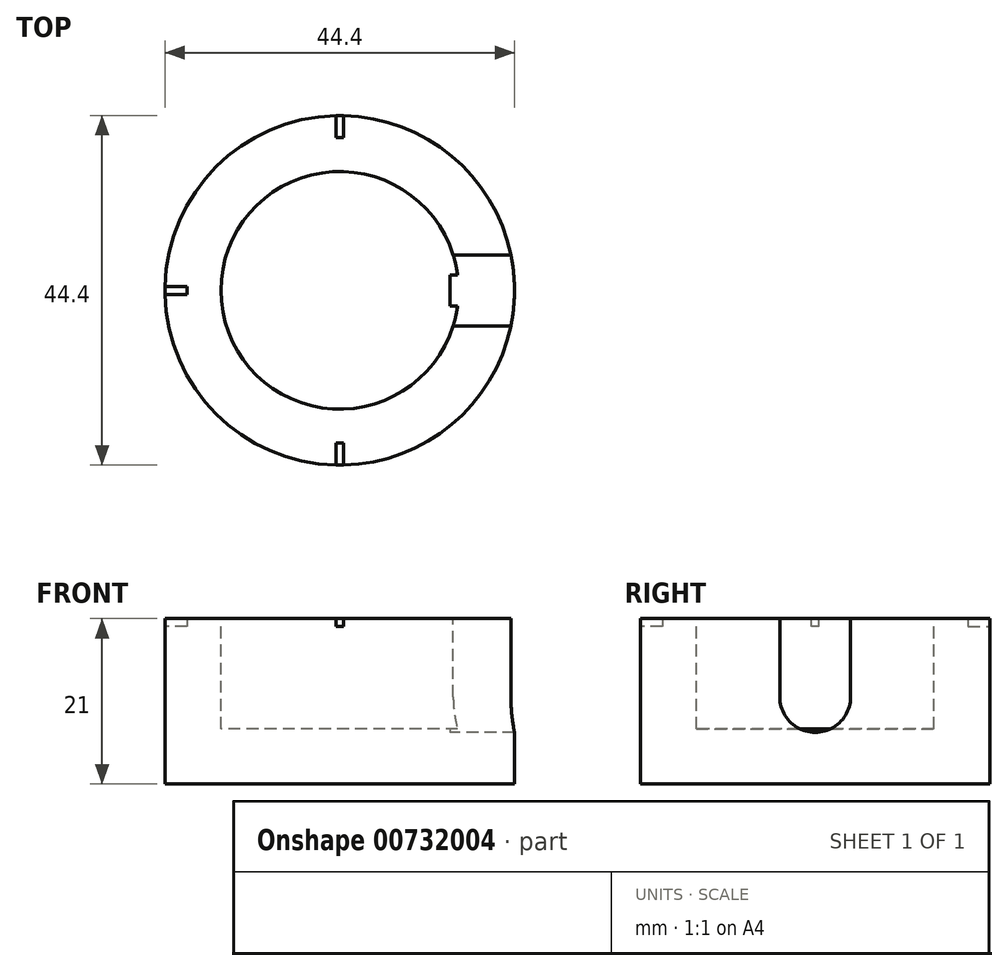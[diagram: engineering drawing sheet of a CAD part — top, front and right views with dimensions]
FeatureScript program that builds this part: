
annotation { "Feature Type Name" : "Feature", "Feature Type Description" : "" }
export const myFeature = defineFeature(function(context is Context, id is Id, definition is map)
    precondition{}
    {
        {
            var Q0;
            Q0=qCreatedBy(makeId("Front.planeOp"),FACE);
            var sketch = newSketch(context, id + "F0", { "sketchPlane" : qUnion([Q0])});
            skLineSegment(sketch, "E0", {"start": v(0, 0) * mm, "end": v(22.2, 0) * mm});
            skLineSegment(sketch, "E1", {"start": v(22.2, 0) * mm, "end": v(22.2, 21) * mm});
            skLineSegment(sketch, "E2", {"start": v(22.2, 21) * mm, "end": v(15.1, 21) * mm});
            skLineSegment(sketch, "E3", {"start": v(15.1, 21) * mm, "end": v(15.1, 7) * mm});
            skLineSegment(sketch, "E4", {"start": v(15.1, 7) * mm, "end": v(0, 7) * mm});
            skLineSegment(sketch, "E5", {"start": v(0, 7) * mm, "end": v(0, 0) * mm});
            skSolve(sketch);
        }
        {
            var Q0;
            Q0=qCreatedBy(makeId("Right.planeOp"),FACE);
            var sketch = newSketch(context, id + "F1", { "sketchPlane" : qUnion([Q0])});
            skLineSegment(sketch, "E6", {"start": v(0, 21.05) * mm, "end": v(-4.5, 21.05) * mm});
            skLineSegment(sketch, "E7", {"start": v(4.5, 21.05) * mm, "end": v(0, 21.05) * mm});
            skLineSegment(sketch, "E8", {"start": v(4.5, 21.05) * mm, "end": v(4.5, 11.05) * mm});
            skLineSegment(sketch, "E9", {"start": v(-4.5, 21.05) * mm, "end": v(-4.5, 11.05) * mm});
            skArc(sketch, "E10", {"start": v(4.5, 11.05) * mm, "mid": v(0, 6.55) * mm, "end": v(-4.5, 11.05) * mm});
            skSolve(sketch);
        }
        {
            var Q0;
            Q0=qCreatedBy(makeId("Top.planeOp"),FACE);
            var sketch = newSketch(context, id + "F2", { "sketchPlane" : qUnion([Q0])});
            skLineSegment(sketch, "E11", {"start": v(0, -19.4) * mm, "end": v(0.5, -19.4) * mm});
            skLineSegment(sketch, "E12", {"start": v(0.5, -19.4) * mm, "end": v(0.5, -22.4) * mm});
            skLineSegment(sketch, "E13", {"start": v(0.5, -22.4) * mm, "end": v(-0.5, -22.4) * mm});
            skLineSegment(sketch, "E14", {"start": v(-0.5, -22.4) * mm, "end": v(-0.5, -19.4) * mm});
            skLineSegment(sketch, "E15", {"start": v(-0.5, -19.4) * mm, "end": v(0, -19.4) * mm});
            skLineSegment(sketch, "E16", {"start": v(0, 22.42) * mm, "end": v(0.5, 22.42) * mm});
            skLineSegment(sketch, "E17", {"start": v(0.5, 22.42) * mm, "end": v(0.5, 19.42) * mm});
            skLineSegment(sketch, "E18", {"start": v(0.5, 19.42) * mm, "end": v(-0.5, 19.42) * mm});
            skLineSegment(sketch, "E19", {"start": v(-0.5, 19.42) * mm, "end": v(-0.5, 22.42) * mm});
            skLineSegment(sketch, "E20", {"start": v(-0.5, 22.42) * mm, "end": v(0, 22.42) * mm});
            skLineSegment(sketch, "E21", {"start": v(22.4, 0) * mm, "end": v(22.4, -0.5) * mm});
            skLineSegment(sketch, "E22", {"start": v(22.4, -0.5) * mm, "end": v(19.4, -0.5) * mm});
            skLineSegment(sketch, "E23", {"start": v(19.4, -0.5) * mm, "end": v(19.4, 0.5) * mm});
            skLineSegment(sketch, "E24", {"start": v(19.4, 0.5) * mm, "end": v(22.4, 0.5) * mm});
            skLineSegment(sketch, "E25", {"start": v(22.4, 0.5) * mm, "end": v(22.4, 0) * mm});
            skLineSegment(sketch, "E26", {"start": v(-19.4, 0) * mm, "end": v(-19.4, -0.5) * mm});
            skLineSegment(sketch, "E27", {"start": v(-19.4, -0.5) * mm, "end": v(-22.4, -0.5) * mm});
            skLineSegment(sketch, "E28", {"start": v(-22.4, -0.5) * mm, "end": v(-22.4, 0.5) * mm});
            skLineSegment(sketch, "E29", {"start": v(-22.4, 0.5) * mm, "end": v(-19.4, 0.5) * mm});
            skLineSegment(sketch, "E30", {"start": v(-19.4, 0.5) * mm, "end": v(-19.4, 0) * mm});
            skSolve(sketch);
        }
        {
            var Q0;
            Q0=makeQuery(id+"F0.imprint","IMPRINT",FACE,{"disambiguationData":[TD([[makeQuery(id+"F0.imprint","IMPRINT",EDGE,{"derivedFrom":sQuery(id+"F0.wireOp",EDGE,"E0")}),1.0]])]});
            var Q1;
            Q1=sQuery(id+"F0.wireOp",EDGE,"E5");
            revolve(context, id + "F3", {"surfaceOperationType" : NewSurfaceOperationType.NEW, "entities" : qUnion([Q0]), "axis" : qUnion([Q1]), "revolveType" : RevolveType.FULL});
        }
        {
            var Q0;
            Q0=makeQuery(id+"F1.imprint","IMPRINT",FACE,{"disambiguationData":[TD([[makeQuery(id+"F1.imprint","IMPRINT",EDGE,{"derivedFrom":sQuery(id+"F1.wireOp",EDGE,"E6")}),1.0]])]});
            extrude(context, id + "F4", {"entities" : qUnion([Q0]), "operationType" : NewBodyOperationType.REMOVE, "depth" : 30 * mm, "offsetDistance" : 25 * mm, "hasSecondDirection" : true, "secondDirectionOppositeDirection" : true, "secondDirectionDepth" : -14 * mm});
        }
        {
            var Q0;
            Q0 = qSketchRegion(id + "F2", true);
            var Q1;
            Q1=sQuery(id+"F2.wireOp",EDGE,"E13");
            var Q2;
            Q2=sQuery(id+"F2.wireOp",EDGE,"E17");
            var Q3;
            Q3=sQuery(id+"F2.wireOp",EDGE,"E18");
            var Q4;
            Q4=sQuery(id+"F2.wireOp",EDGE,"E12");
            var Q5;
            Q5=sQuery(id+"F2.wireOp",EDGE,"E14");
            var Q6;
            Q6=sQuery(id+"F2.wireOp",EDGE,"E19");
            var Q7;
            Q7=sQuery(id+"F2.wireOp",EDGE,"E27");
            var Q8;
            Q8=sQuery(id+"F2.wireOp",EDGE,"E29");
            var Q9;
            Q9=sQuery(id+"F2.wireOp",EDGE,"E24");
            var Q10;
            Q10=sQuery(id+"F2.wireOp",EDGE,"E22");
            var Q11;
            Q11=sQuery(id+"F2.wireOp",EDGE,"E28");
            var Q12;
            Q12=sQuery(id+"F2.wireOp",EDGE,"E23");
            var Q13;
            Q13=sQuery(id+"F2.wireOp",EDGE,"E25");
            var Q14;
            Q14=sQuery(id+"F2.wireOp",EDGE,"E16");
            var Q15;
            Q15=sQuery(id+"F2.wireOp",EDGE,"E15");
            var Q16;
            Q16=sQuery(id+"F2.wireOp",EDGE,"E11");
            var Q17;
            Q17=sQuery(id+"F2.wireOp",EDGE,"E20");
            var Q18;
            Q18=sQuery(id+"F2.wireOp",EDGE,"E30");
            var Q19;
            Q19=sQuery(id+"F2.wireOp",EDGE,"E21");
            var Q20;
            Q20=sQuery(id+"F2.wireOp",EDGE,"E26");
            extrude(context, id + "F5", {"entities" : qUnion([Q0]), "operationType" : NewBodyOperationType.REMOVE, "surfaceEntities" : qUnion([Q1, Q2, Q3, Q4, Q5, Q6, Q7, Q8, Q9, Q10, Q11, Q12, Q13, Q14, Q15, Q16, Q17, Q18, Q19, Q20]), "depth" : 21 * mm, "offsetDistance" : 25 * mm, "hasSecondDirection" : true, "secondDirectionOppositeDirection" : false, "secondDirectionDepth" : 20 * mm});
        }
    });
